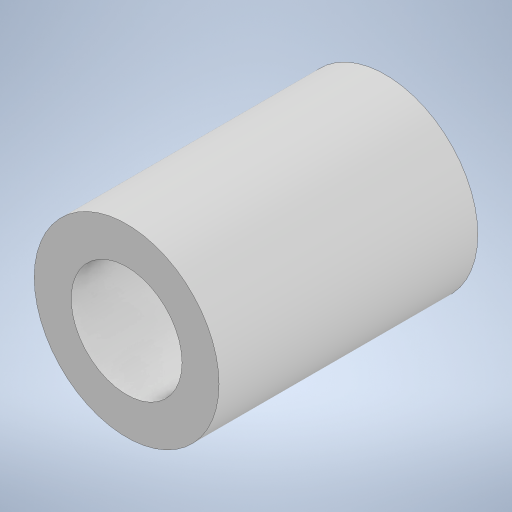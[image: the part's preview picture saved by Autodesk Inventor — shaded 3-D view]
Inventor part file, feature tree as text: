
AUTODESK INVENTOR PART (.ipt)
format: ipt  version: 2023 (Build 270158000, 158)  size: 202,240 bytes
history: native  units: mm
features: extrude x1, sketch x1
ambient origin geometry x8: Origin, YZ Plane, XZ Plane, XY Plane, X Axis, Y Axis, Z Axis, Center Point
bodies: Solid1 (feature_tree)
feature tree (2):
  extrude  "Extrusion1"  Depth=10.0mm
  sketch  "Sketch1"  dims[d0=6.0mm d1=10.0mm d2=14.0mm d3=0.0mm]
